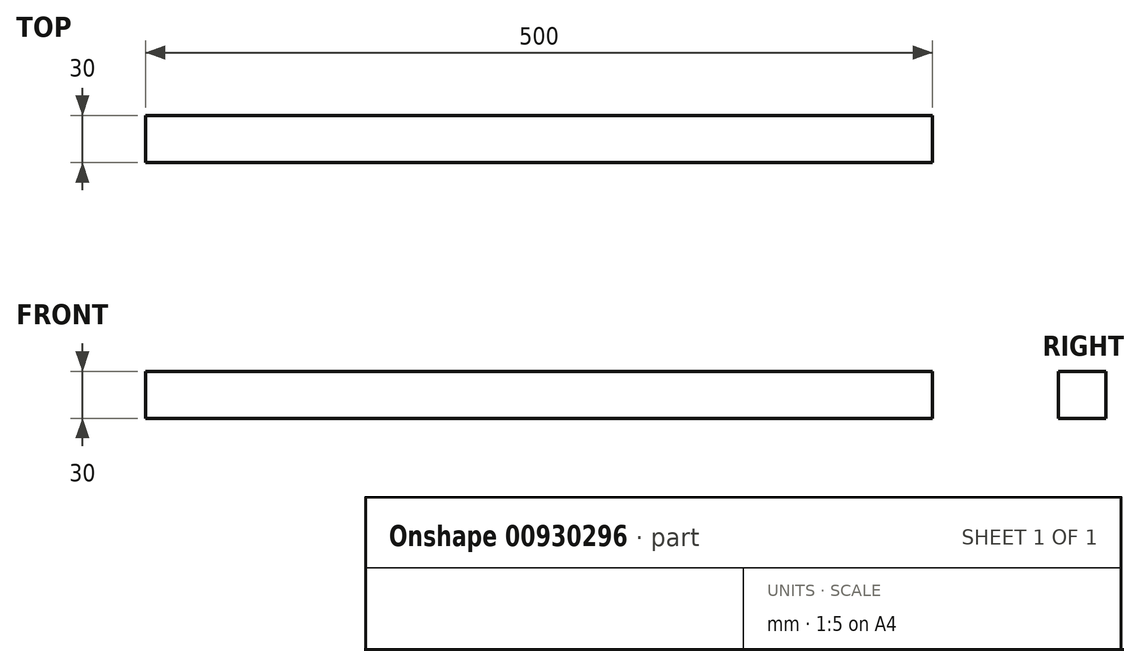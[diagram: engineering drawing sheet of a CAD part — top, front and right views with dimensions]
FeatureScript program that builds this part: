
annotation { "Feature Type Name" : "Feature", "Feature Type Description" : "" }
export const myFeature = defineFeature(function(context is Context, id is Id, definition is map)
    precondition{}
    {
        {
            var Q0;
            Q0=qCreatedBy(makeId("Top.planeOp"),FACE);
            var sketch = newSketch(context, id + "F0", { "sketchPlane" : qUnion([Q0])});
            skLineSegment(sketch, "E0.bottom", {"start": v(-249.72, -70.55) * mm, "end": v(250.28, -70.55) * mm});
            skLineSegment(sketch, "E0.top", {"start": v(-249.72, -100.55) * mm, "end": v(250.28, -100.55) * mm});
            skLineSegment(sketch, "E0.left", {"start": v(-249.72, -70.55) * mm, "end": v(-249.72, -100.55) * mm});
            skLineSegment(sketch, "E0.right", {"start": v(250.28, -70.55) * mm, "end": v(250.28, -100.55) * mm});
            skSolve(sketch);
        }
        {
            var Q0;
            Q0 = qSketchRegion(id + "F0", true);
            extrude(context, id + "F1", {"entities" : qUnion([Q0]), "depth" : 30 * mm, "offsetDistance" : 25 * mm});
        }
    });
